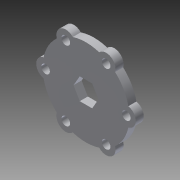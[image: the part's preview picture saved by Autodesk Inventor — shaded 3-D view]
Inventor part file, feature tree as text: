
AUTODESK INVENTOR PART (.ipt)
format: ipt  version: 2014 SP1 (Build 180222100, 222)  size: 142,336 bytes
history: native  units: in
note: dims shown in document units (in); Inventor stores cm internally (conversion verified against a paired STEP export)
features: extrude x1, sketch x1, reference x1
ambient origin geometry x8: Origin, YZ Plane, XZ Plane, XY Plane, X Axis, Y Axis, Z Axis, Center Point
bodies: Solid1 (feature_tree)
feature tree (3):
  extrude  "Extrusion1"  Depth=0.1875in TaperAngle=0.0deg
  sketch  "Sketch1"  dims[d0=0.5in d1=0.1875in d2=0.0in]
  reference  "Reference2"
